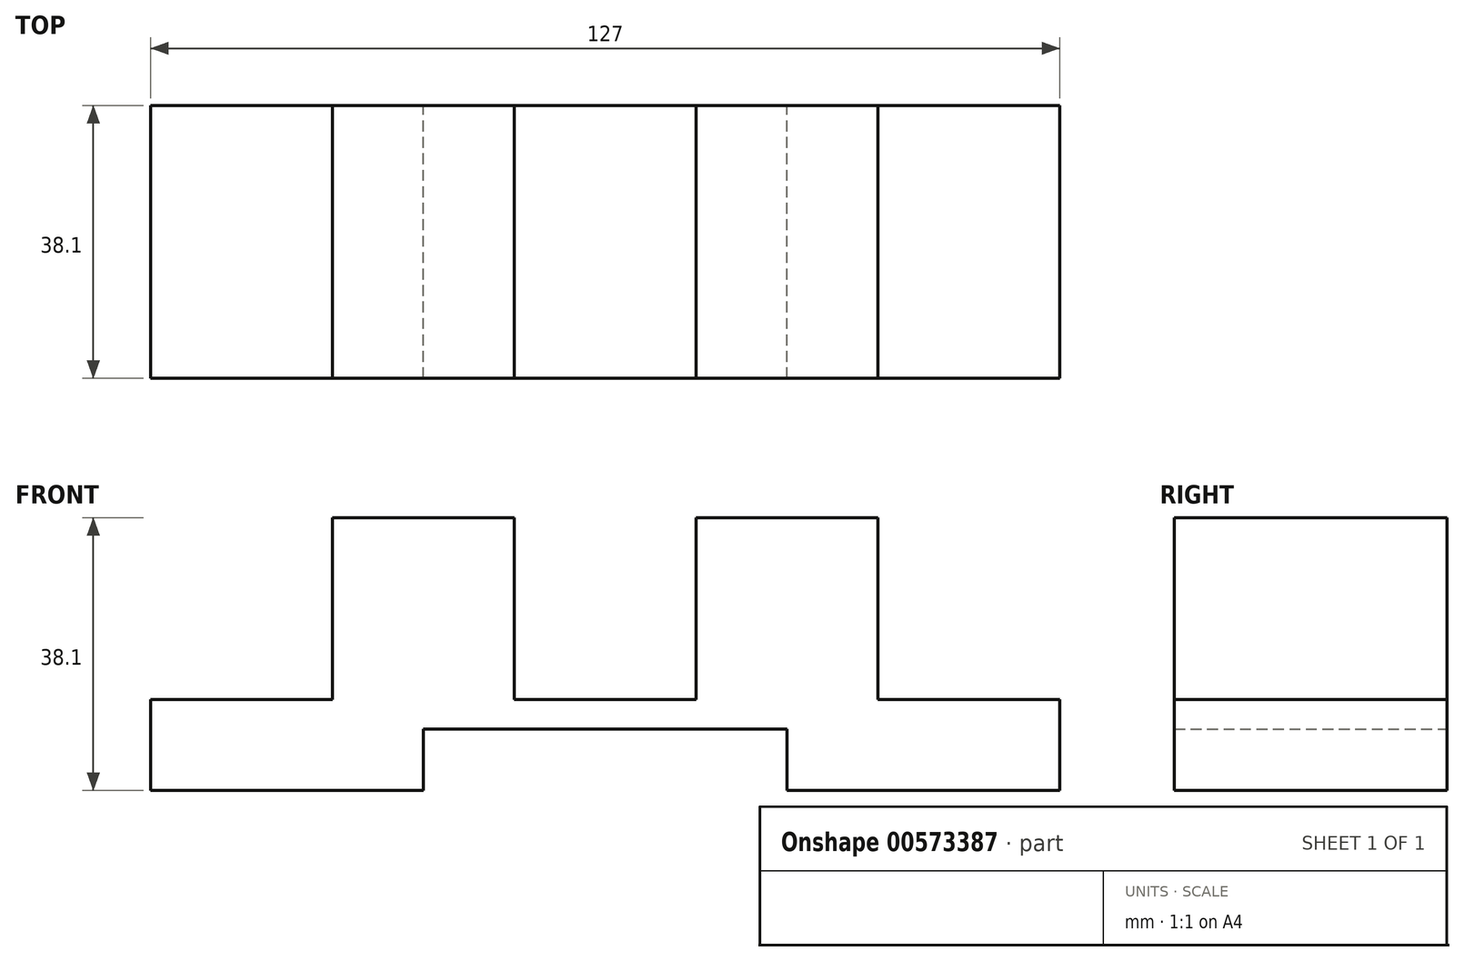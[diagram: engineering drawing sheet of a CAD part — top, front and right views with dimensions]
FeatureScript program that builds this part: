
annotation { "Feature Type Name" : "Feature", "Feature Type Description" : "" }
export const myFeature = defineFeature(function(context is Context, id is Id, definition is map)
    precondition{}
    {
        {
            var Q0;
            Q0=qCreatedBy(makeId("Front.planeOp"),FACE);
            var sketch = newSketch(context, id + "F0", { "sketchPlane" : qUnion([Q0])});
            skLineSegment(sketch, "E0", {"start": v(-56.67, -24.34) * mm, "end": v(-56.67, -11.64) * mm});
            skLineSegment(sketch, "E1", {"start": v(-56.67, -11.64) * mm, "end": v(-31.27, -11.64) * mm});
            skLineSegment(sketch, "E2", {"start": v(-31.27, -11.64) * mm, "end": v(-31.27, 13.76) * mm});
            skLineSegment(sketch, "E3", {"start": v(-31.27, 13.76) * mm, "end": v(-5.87, 13.76) * mm});
            skLineSegment(sketch, "E4", {"start": v(-5.87, 13.76) * mm, "end": v(-5.87, -11.64) * mm});
            skLineSegment(sketch, "E5", {"start": v(19.53, -11.64) * mm, "end": v(19.53, 13.76) * mm});
            skLineSegment(sketch, "E6", {"start": v(19.53, 13.76) * mm, "end": v(44.93, 13.76) * mm});
            skLineSegment(sketch, "E7", {"start": v(44.93, -11.64) * mm, "end": v(44.93, 13.76) * mm});
            skLineSegment(sketch, "E8", {"start": v(-5.87, -11.64) * mm, "end": v(19.53, -11.64) * mm});
            skLineSegment(sketch, "E9", {"start": v(44.93, -11.64) * mm, "end": v(70.33, -11.64) * mm});
            skLineSegment(sketch, "E10", {"start": v(70.33, -11.64) * mm, "end": v(70.33, -24.34) * mm});
            skLineSegment(sketch, "E11", {"start": v(32.23, -24.34) * mm, "end": v(70.33, -24.34) * mm});
            skLineSegment(sketch, "E12", {"start": v(32.23, -24.34) * mm, "end": v(32.23, -15.75) * mm});
            skLineSegment(sketch, "E13", {"start": v(-18.57, -15.75) * mm, "end": v(32.23, -15.75) * mm});
            skLineSegment(sketch, "E14", {"start": v(-18.57, -15.75) * mm, "end": v(-18.57, -24.34) * mm});
            skLineSegment(sketch, "E15", {"start": v(-56.67, -24.34) * mm, "end": v(-18.57, -24.34) * mm});
            skSolve(sketch);
        }
        {
            var Q0;
            Q0=makeQuery(id+"F0.imprint","IMPRINT",FACE,{"disambiguationData":[TD([[makeQuery(id+"F0.imprint","IMPRINT",EDGE,{"derivedFrom":sQuery(id+"F0.wireOp",EDGE,"E0")}),-1.0]])]});
            extrude(context, id + "F1", {"entities" : qUnion([Q0]), "depth" : 38.1 * mm, "offsetDistance" : 25.4 * mm});
        }
    });
